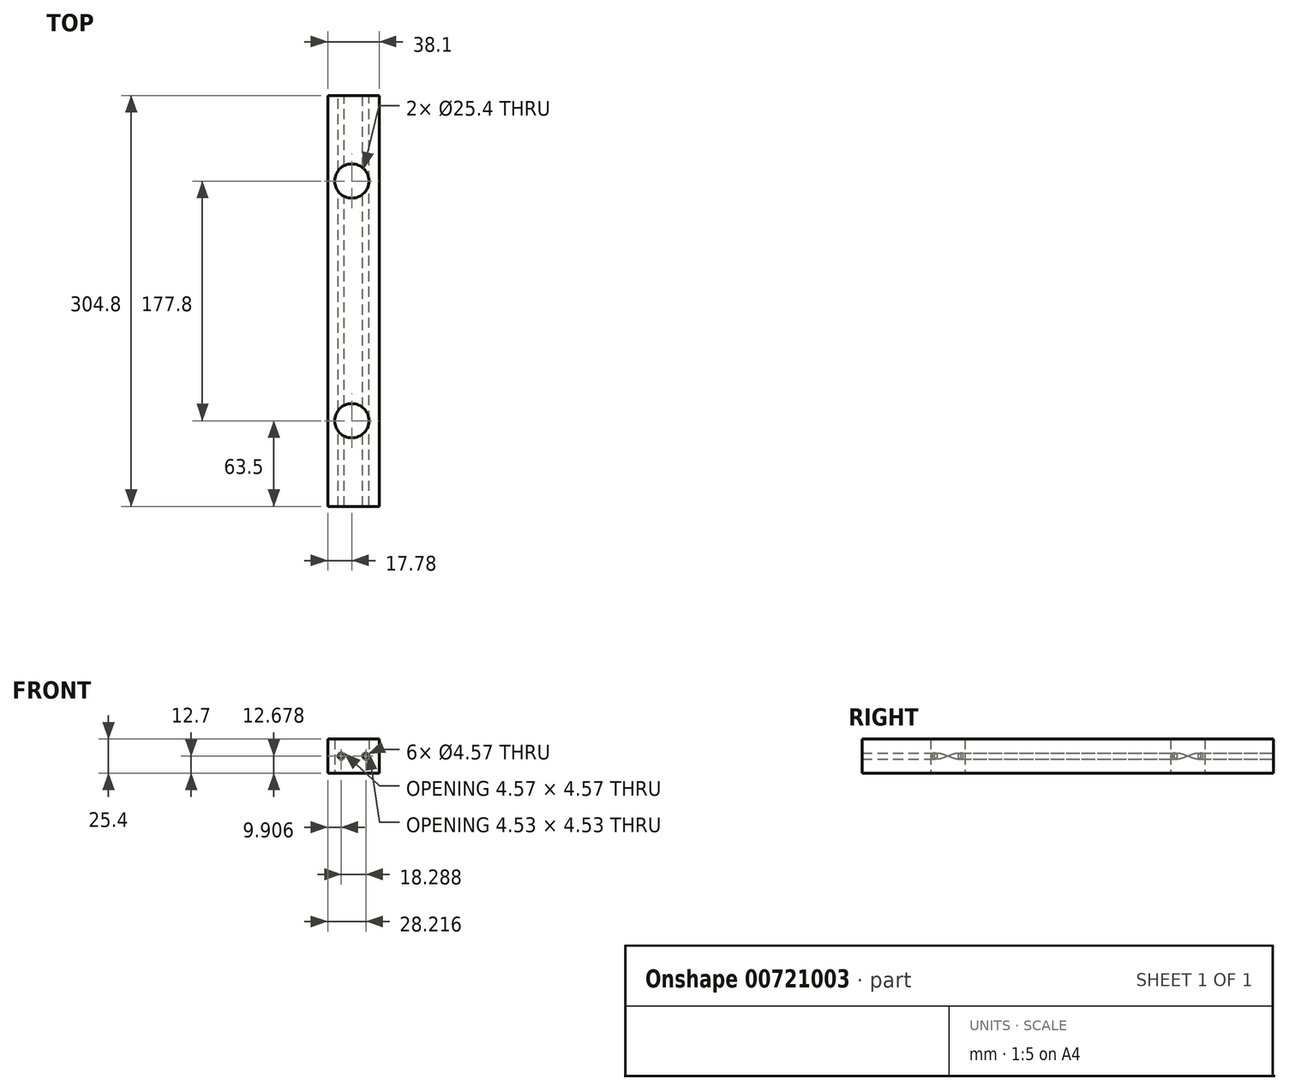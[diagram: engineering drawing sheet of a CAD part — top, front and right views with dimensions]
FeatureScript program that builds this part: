
annotation { "Feature Type Name" : "Feature", "Feature Type Description" : "" }
export const myFeature = defineFeature(function(context is Context, id is Id, definition is map)
    precondition{}
    {
        {
            var Q0;
            Q0=qCreatedBy(makeId("Front.planeOp"),FACE);
            var sketch = newSketch(context, id + "F0", { "sketchPlane" : qUnion([Q0])});
            skLineSegment(sketch, "E0", {"start": v(0, 0) * mm, "end": v(0, 25.4) * mm});
            skLineSegment(sketch, "E1", {"start": v(0, 25.4) * mm, "end": v(38.1, 25.4) * mm});
            skLineSegment(sketch, "E2", {"start": v(38.1, 25.4) * mm, "end": v(38.1, 0) * mm});
            skLineSegment(sketch, "E3", {"start": v(38.1, 0) * mm, "end": v(0, 0) * mm});
            skCircle(sketch, "E4", {"center": v(9.9, 12.7) * mm, "radius": 2.29 * mm});
            skCircle(sketch, "E5", {"center": v(28.2, 12.7) * mm, "radius": 2.29 * mm});
            skSolve(sketch);
        }
        {
            var Q0;
            Q0 = qSketchRegion(id + "F0", true);
            extrude(context, id + "F1", {"entities" : qUnion([Q0]), "depth" : 304.8 * mm, "offsetDistance" : 25.4 * mm});
        }
        {
            var Q0;
            Q0=qCreatedBy(makeId("Top.planeOp"),FACE);
            var sketch = newSketch(context, id + "F2", { "sketchPlane" : qUnion([Q0])});
            skCircle(sketch, "E6", {"center": v(17.78, -241.3) * mm, "radius": 12.7 * mm});
            skCircle(sketch, "E7", {"center": v(17.78, -63.5) * mm, "radius": 12.7 * mm});
            skSolve(sketch);
        }
        {
            var Q0;
            Q0 = qSketchRegion(id + "F2", true);
            extrude(context, id + "F3", {"entities" : qUnion([Q0]), "operationType" : NewBodyOperationType.REMOVE, "endBound" : BoundingType.THROUGH_ALL, "depth" : 207.52 * mm, "offsetDistance" : 25.4 * mm});
        }
    });
